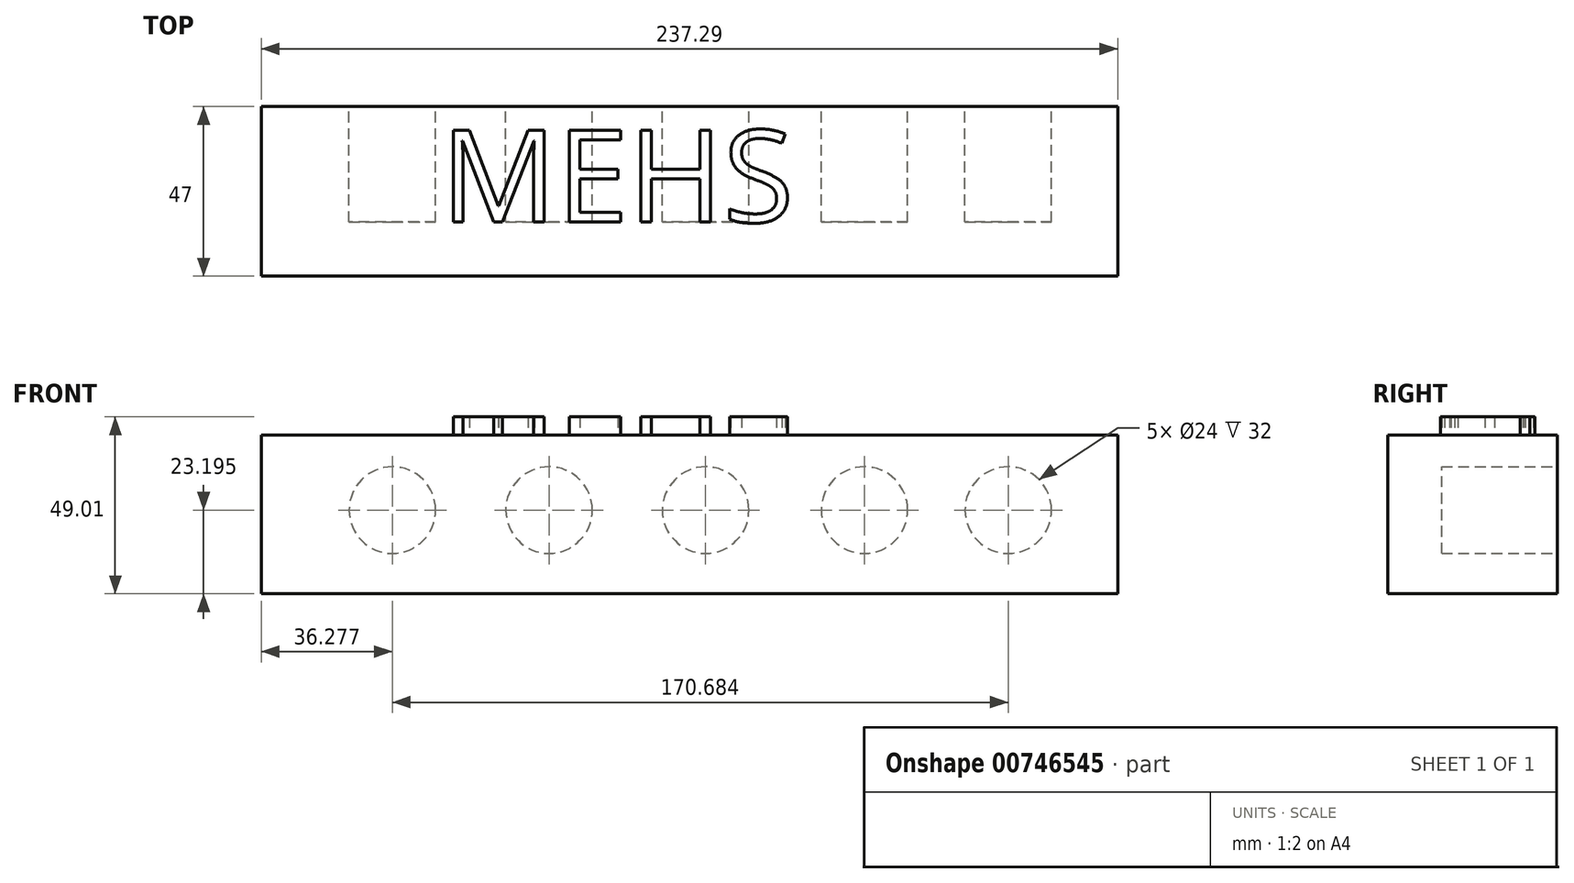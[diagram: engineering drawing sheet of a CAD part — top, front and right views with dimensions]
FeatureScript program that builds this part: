
annotation { "Feature Type Name" : "Feature", "Feature Type Description" : "" }
export const myFeature = defineFeature(function(context is Context, id is Id, definition is map)
    precondition{}
    {
        {
            var Q0;
            Q0=qCreatedBy(makeId("Front.planeOp"),FACE);
            var sketch = newSketch(context, id + "F0", { "sketchPlane" : qUnion([Q0])});
            skCircle(sketch, "E0", {"center": v(44.9, 8.91) * mm, "radius": 12 * mm});
            skCircle(sketch, "E1", {"center": v(-125.78, 8.91) * mm, "radius": 12 * mm});
            skCircle(sketch, "E2", {"center": v(-82.37, 8.91) * mm, "radius": 12 * mm});
            skCircle(sketch, "E3", {"center": v(-38.95, 8.91) * mm, "radius": 12 * mm});
            skCircle(sketch, "E4", {"center": v(5.06, 8.91) * mm, "radius": 12 * mm});
            skLineSegment(sketch, "E5.bottom", {"start": v(-162.06, 29.73) * mm, "end": v(75.23, 29.73) * mm});
            skLineSegment(sketch, "E5.top", {"start": v(-162.06, -14.28) * mm, "end": v(75.23, -14.28) * mm});
            skLineSegment(sketch, "E5.left", {"start": v(-162.06, 29.73) * mm, "end": v(-162.06, -14.28) * mm});
            skLineSegment(sketch, "E5.right", {"start": v(75.23, 29.73) * mm, "end": v(75.23, -14.28) * mm});
            skSolve(sketch);
        }
        {
            var Q0;
            Q0 = qSketchRegion(id + "F0", true);
            extrude(context, id + "F1", {"entities" : qUnion([Q0]), "depth" : 32 * mm, "offsetDistance" : 25 * mm});
        }
        {
            var Q0;
            Q0=makeQuery(id+"F1.opExtrude","SWEPT_FACE",FACE,{"disambiguationData":[OSD([sQuery(id+"F0.wireOp",EDGE,"E5.bottom")])]});
            var sketch = newSketch(context, id + "F2", { "sketchPlane" : qUnion([Q0])});
            skText(sketch, "E6", { "text": "MEHS\n", "fontName": "OpenSans-Regular.ttf"});
            const initialGuessF2  = {"E6": [-0.1124, -0.032, 1, 0, 0.02565]};
            skSetInitialGuess(sketch, initialGuessF2);
            skSolve(sketch);
        }
        {
            var Q0;
            Q0 = qSketchRegion(id + "F2", true);
            extrude(context, id + "F3", {"entities" : qUnion([Q0]), "operationType" : NewBodyOperationType.ADD, "depth" : 5 * mm, "offsetDistance" : 25 * mm});
        }
        {
            var Q0;
            Q0=makeQuery(id+"F3.boolean.opBoolean","MERGE",FACE,{"derivedFrom":[makeQuery(id+"F1.opExtrude","CAP_FACE",FACE,{"disambiguationData":[OSD([sQuery(id+"F0.wireOp",EDGE,"E0"),sQuery(id+"F0.wireOp",EDGE,"E1"),sQuery(id+"F0.wireOp",EDGE,"E2"),sQuery(id+"F0.wireOp",EDGE,"E3"),sQuery(id+"F0.wireOp",EDGE,"E4"),sQuery(id+"F0.wireOp",EDGE,"E5.bottom"),sQuery(id+"F0.wireOp",EDGE,"E5.top"),sQuery(id+"F0.wireOp",EDGE,"E5.left"),sQuery(id+"F0.wireOp",EDGE,"E5.right")])],"isStart":false}),makeQuery(id+"F3.opExtrude","SWEPT_FACE",FACE,{"disambiguationData":[OSD([sQuery(id+"F2.wireOp",EDGE,"E6.sketch_text.stroke-4")])]}),makeQuery(id+"F3.opExtrude","SWEPT_FACE",FACE,{"disambiguationData":[OSD([sQuery(id+"F2.wireOp",EDGE,"E6.sketch_text.stroke-12")])]}),makeQuery(id+"F3.opExtrude","SWEPT_FACE",FACE,{"disambiguationData":[OSD([sQuery(id+"F2.wireOp",EDGE,"E6.sketch_text.stroke-17")])]}),makeQuery(id+"F3.opExtrude","SWEPT_FACE",FACE,{"disambiguationData":[OSD([sQuery(id+"F2.wireOp",EDGE,"E6.sketch_text.stroke-18")])]}),makeQuery(id+"F3.opExtrude","SWEPT_FACE",FACE,{"disambiguationData":[OSD([sQuery(id+"F2.wireOp",EDGE,"E6.sketch_text.stroke-30")])]}),makeQuery(id+"F3.opExtrude","SWEPT_FACE",FACE,{"disambiguationData":[OSD([sQuery(id+"F2.wireOp",EDGE,"E6.sketch_text.stroke-34")])]})]});
            var sketch = newSketch(context, id + "F4", { "sketchPlane" : qUnion([Q0])});
            skLineSegment(sketch, "E7.bottom", {"start": v(-162.06, 29.73) * mm, "end": v(75.23, 29.73) * mm});
            skLineSegment(sketch, "E7.top", {"start": v(-162.06, -14.28) * mm, "end": v(75.23, -14.28) * mm});
            skLineSegment(sketch, "E7.left", {"start": v(-162.06, 29.73) * mm, "end": v(-162.06, -14.28) * mm});
            skLineSegment(sketch, "E7.right", {"start": v(75.23, 29.73) * mm, "end": v(75.23, -14.28) * mm});
            skSolve(sketch);
        }
        {
            var Q0;
            Q0 = qSketchRegion(id + "F4", true);
            extrude(context, id + "F5", {"entities" : qUnion([Q0]), "operationType" : NewBodyOperationType.ADD, "depth" : 15 * mm, "offsetDistance" : 25 * mm});
        }
    });
